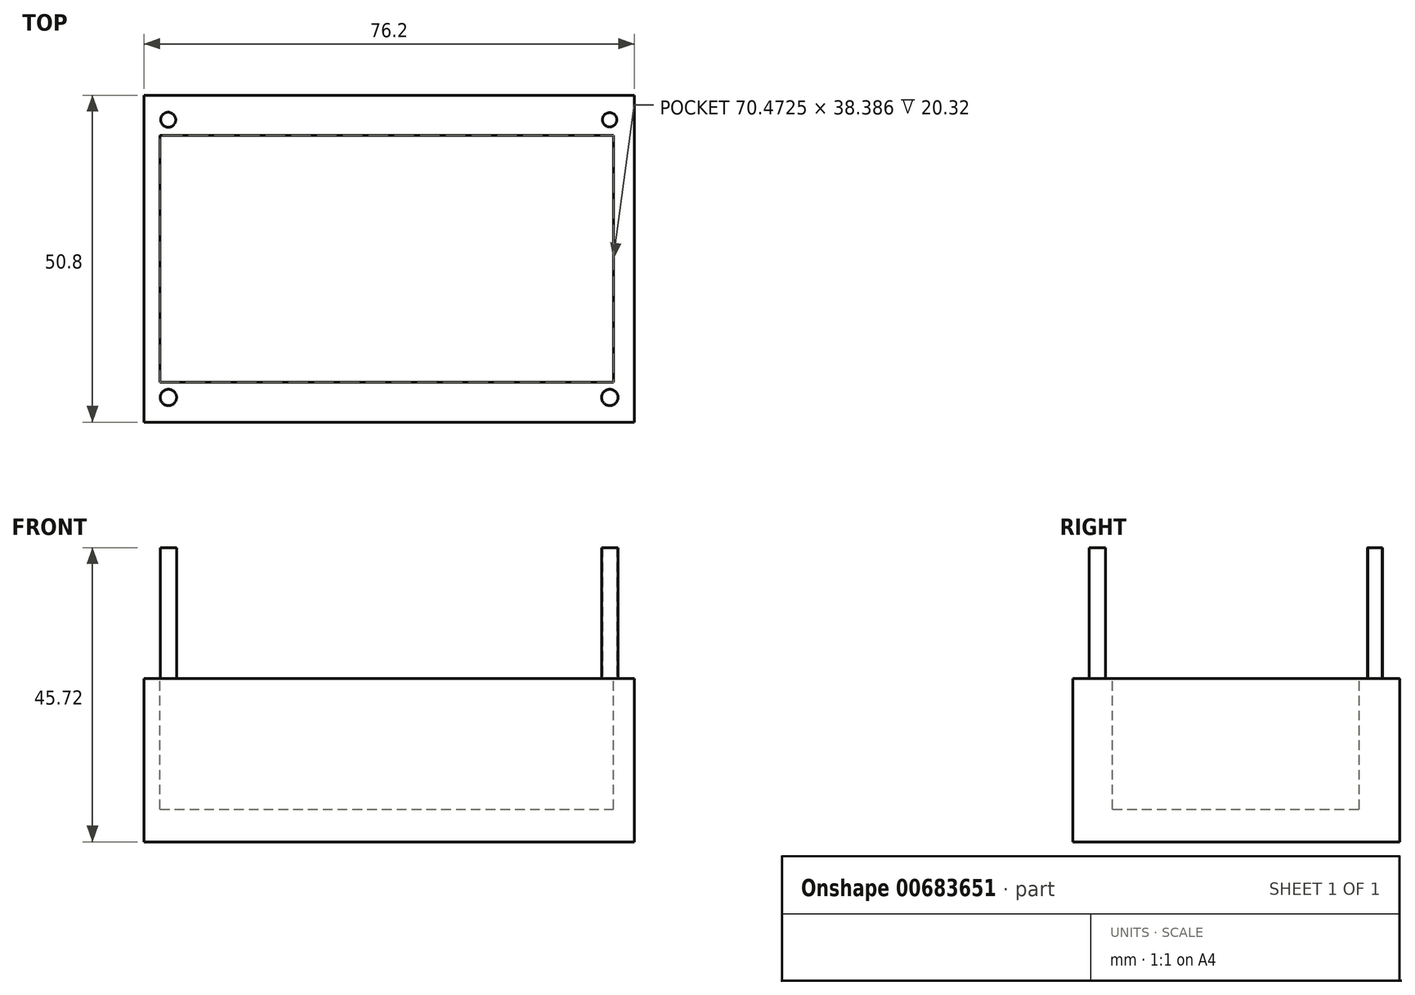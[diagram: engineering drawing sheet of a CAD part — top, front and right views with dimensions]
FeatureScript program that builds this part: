
annotation { "Feature Type Name" : "Feature", "Feature Type Description" : "" }
export const myFeature = defineFeature(function(context is Context, id is Id, definition is map)
    precondition{}
    {
        {
            var Q0;
            Q0=qCreatedBy(makeId("Top.planeOp"),FACE);
            var sketch = newSketch(context, id + "F0", { "sketchPlane" : qUnion([Q0])});
            skLineSegment(sketch, "E0.bottom", {"start": v(0, 0) * mm, "end": v(76.2, 0) * mm});
            skLineSegment(sketch, "E0.top", {"start": v(0, 50.8) * mm, "end": v(76.2, 50.8) * mm});
            skLineSegment(sketch, "E0.left", {"start": v(0, 0) * mm, "end": v(0, 50.8) * mm});
            skLineSegment(sketch, "E0.right", {"start": v(76.2, 0) * mm, "end": v(76.2, 50.8) * mm});
            skSolve(sketch);
        }
        {
            var Q0;
            Q0=makeQuery(id+"F0.imprint","IMPRINT",FACE,{"disambiguationData":[TD([[makeQuery(id+"F0.imprint","IMPRINT",EDGE,{"derivedFrom":sQuery(id+"F0.wireOp",EDGE,"E0.bottom")}),1.0]])]});
            extrude(context, id + "F1", {"entities" : qUnion([Q0]), "oppositeDirection" : true, "depth" : 25.4 * mm, "offsetDistance" : 25.4 * mm});
        }
        {
            var Q0;
            Q0=qCreatedBy(makeId("Top.planeOp"),FACE);
            var sketch = newSketch(context, id + "F2", { "sketchPlane" : qUnion([Q0])});
            skLineSegment(sketch, "E1.bottom", {"start": v(2.5, 6.18) * mm, "end": v(72.97, 6.18) * mm});
            skLineSegment(sketch, "E1.top", {"start": v(2.5, 44.56) * mm, "end": v(72.97, 44.56) * mm});
            skLineSegment(sketch, "E1.left", {"start": v(2.5, 6.18) * mm, "end": v(2.5, 44.56) * mm});
            skLineSegment(sketch, "E1.right", {"start": v(72.97, 6.18) * mm, "end": v(72.97, 44.56) * mm});
            skSolve(sketch);
        }
        {
            var Q0;
            Q0=makeQuery(id+"F2.imprint","IMPRINT",FACE,{"disambiguationData":[TD([[makeQuery(id+"F2.imprint","IMPRINT",EDGE,{"derivedFrom":sQuery(id+"F2.wireOp",EDGE,"E1.bottom")}),1.0]])]});
            extrude(context, id + "F3", {"entities" : qUnion([Q0]), "operationType" : NewBodyOperationType.REMOVE, "oppositeDirection" : true, "depth" : 20.32 * mm, "offsetDistance" : 25.4 * mm});
        }
        {
            var Q0;
            Q0=qCreatedBy(makeId("Top.planeOp"),FACE);
            var sketch = newSketch(context, id + "F4", { "sketchPlane" : qUnion([Q0])});
            skCircle(sketch, "E2", {"center": v(3.78, 46.98) * mm, "radius": 1.16 * mm});
            skCircle(sketch, "E3", {"center": v(72.36, 46.97) * mm, "radius": 1.12 * mm});
            skCircle(sketch, "E4", {"center": v(72.4, 3.83) * mm, "radius": 1.27 * mm});
            skCircle(sketch, "E5", {"center": v(3.8, 3.83) * mm, "radius": 1.27 * mm});
            skSolve(sketch);
        }
        {
            var Q0;
            Q0 = qSketchRegion(id + "F4", true);
            extrude(context, id + "F5", {"entities" : qUnion([Q0]), "operationType" : NewBodyOperationType.ADD, "depth" : 20.32 * mm, "offsetDistance" : 25.4 * mm});
        }
    });
